# Revit family: Gira_126066
name_source: partatom
category: Electrical Fixtures
revit_build: Autodesk Revit 2017 (Build: 20160225_1515(x64)
units: mm (PartAtom-declared; Revit-internal decimal feet)

## family parameters
Cut with Voids When Loaded = No
Host = Face
Maintain Annotation Orientation = Yes
Part Type = Normal
Room Calculation Point = No
Round Connector Dimension = Use Diameter
Shared = No

## types (1)
- Türstation 1f UP Gira TX_44 (WG UP) Reinweiß
    Anzahl der Ruftasten = 1
    Available = Yes
    Category = Türstation für Türkommunikation
    Data sheet (1) = https://katalog.gira.de
    Default Elevation = 1219 mm
    Farbe = weiß
    GTIN = 4010337260660
    HAN = 126066
    HeinzeBIM = https://bimportal.heinze.de
    Installationstechnik = Bus-System
    Keynote = TX44_Komplettgerät_Schalten und Tasten
    Manufacturer URL = https://www.gira.de
    Mit Abdeckung = Yes
    Mit Infoschild = Yes
    Mit Kamera = No
    Modulare Bauweise = Yes
    Montageart = unter Putz
    Name = Türstation 1f UP Gira TX_44 (WG UP) Reinweiß
    Region = DE
    Schutz gegen Vandalismus = Yes
    URL = http://katalog.gira.de

## geometry (parser evidence)
native form markers: Blend x2, Sweep x3
no freeform markers — native parametric forms only
